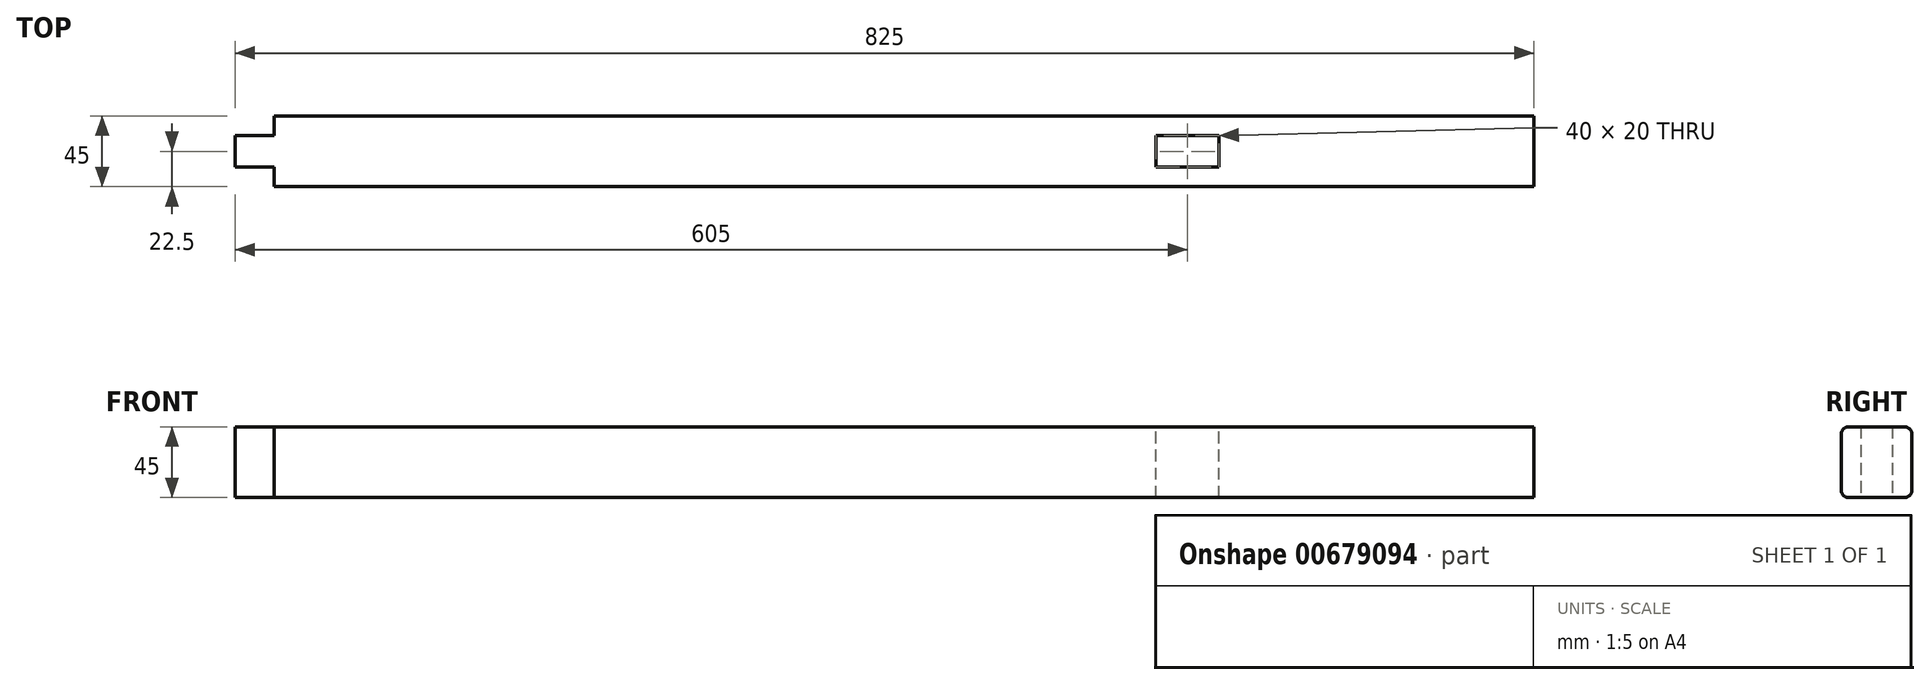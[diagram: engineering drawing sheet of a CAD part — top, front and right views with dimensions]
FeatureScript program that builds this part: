
annotation { "Feature Type Name" : "Feature", "Feature Type Description" : "" }
export const myFeature = defineFeature(function(context is Context, id is Id, definition is map)
    precondition{}
    {
        {
            var Q0;
            Q0=qCreatedBy(makeId("Right.planeOp"),FACE);
            var sketch = newSketch(context, id + "F0", { "sketchPlane" : qUnion([Q0])});
            skLineSegment(sketch, "E0.bottom", {"start": v(22.5, 22.5) * mm, "end": v(-22.5, 22.5) * mm});
            skLineSegment(sketch, "E0.top", {"start": v(22.5, -22.5) * mm, "end": v(-22.5, -22.5) * mm});
            skLineSegment(sketch, "E0.left", {"start": v(22.5, 22.5) * mm, "end": v(22.5, -22.5) * mm});
            skLineSegment(sketch, "E0.right", {"start": v(-22.5, 22.5) * mm, "end": v(-22.5, -22.5) * mm});
            skPoint(sketch, "E0.middle", {"position": v(0, 0) * mm});
            skSolve(sketch);
        }
        {
            var Q0;
            Q0 = qSketchRegion(id + "F0", true);
            extrude(context, id + "F1", {"entities" : qUnion([Q0]), "endBound" : BoundingType.SYMMETRIC, "depth" : 800 * mm, "offsetDistance" : 25 * mm});
        }
        {
            var Q0;
            Q0=makeQuery(id+"F1.opExtrude","CAP_FACE",FACE,{"disambiguationData":[OSD([sQuery(id+"F0.wireOp",EDGE,"E0.bottom"),sQuery(id+"F0.wireOp",EDGE,"E0.top"),sQuery(id+"F0.wireOp",EDGE,"E0.left"),sQuery(id+"F0.wireOp",EDGE,"E0.right")])],"isStart":true});
            var sketch = newSketch(context, id + "F2", { "sketchPlane" : qUnion([Q0])});
            skLineSegment(sketch, "E1.bottom", {"start": v(10, 22.5) * mm, "end": v(-10, 22.5) * mm});
            skLineSegment(sketch, "E1.top", {"start": v(10, -22.5) * mm, "end": v(-10, -22.5) * mm});
            skLineSegment(sketch, "E1.left", {"start": v(10, 22.5) * mm, "end": v(10, -22.5) * mm});
            skLineSegment(sketch, "E1.right", {"start": v(-10, 22.5) * mm, "end": v(-10, -22.5) * mm});
            skPoint(sketch, "E1.middle", {"position": v(0, 0) * mm});
            skSolve(sketch);
        }
        {
            var Q0;
            Q0 = qSketchRegion(id + "F2", true);
            extrude(context, id + "F3", {"entities" : qUnion([Q0]), "operationType" : NewBodyOperationType.ADD, "depth" : 25 * mm, "offsetDistance" : 25 * mm});
        }
        {
            var Q0;
            Q0=makeQuery(id+"F1.opExtrude","SWEPT_EDGE",EDGE,{"disambiguationData":[OSD([sQuery(id+"F0.wireOp",EDGE,"E0.top"),sQuery(id+"F0.wireOp",EDGE,"E0.right")])]});
            var Q1;
            Q1=makeQuery(id+"F1.opExtrude","SWEPT_EDGE",EDGE,{"disambiguationData":[OSD([sQuery(id+"F0.wireOp",EDGE,"E0.top"),sQuery(id+"F0.wireOp",EDGE,"E0.left")])]});
            var Q2;
            Q2=makeQuery(id+"F1.opExtrude","SWEPT_EDGE",EDGE,{"disambiguationData":[OSD([sQuery(id+"F0.wireOp",EDGE,"E0.bottom"),sQuery(id+"F0.wireOp",EDGE,"E0.right")])]});
            var Q3;
            Q3=makeQuery(id+"F1.opExtrude","SWEPT_EDGE",EDGE,{"disambiguationData":[OSD([sQuery(id+"F0.wireOp",EDGE,"E0.bottom"),sQuery(id+"F0.wireOp",EDGE,"E0.left")])]});
            fillet(context, id + "F4", {"entities" : qUnion([Q0, Q1, Q2, Q3]), "radius" : 5 * mm, "tangentPropagation" : true, "allowEdgeOverflow" : false});
        }
        {
            var Q0;
            Q0=makeQuery(id+"F3.boolean.opBoolean","MERGE",FACE,{"derivedFrom":[makeQuery(id+"F1.opExtrude","SWEPT_FACE",FACE,{"disambiguationData":[OSD([sQuery(id+"F0.wireOp",EDGE,"E0.bottom")])]}),makeQuery(id+"F3.opExtrude","SWEPT_FACE",FACE,{"disambiguationData":[OSD([sQuery(id+"F2.wireOp",EDGE,"E1.bottom")])]})]});
            var sketch = newSketch(context, id + "F5", { "sketchPlane" : qUnion([Q0])});
            skLineSegment(sketch, "E2.bottom", {"start": v(200, 10) * mm, "end": v(160, 10) * mm});
            skLineSegment(sketch, "E2.top", {"start": v(200, -10) * mm, "end": v(160, -10) * mm});
            skLineSegment(sketch, "E2.left", {"start": v(200, 10) * mm, "end": v(200, -10) * mm});
            skLineSegment(sketch, "E2.right", {"start": v(160, 10) * mm, "end": v(160, -10) * mm});
            skPoint(sketch, "E2.middle", {"position": v(180, 0) * mm});
            skSolve(sketch);
        }
        {
            var Q0;
            Q0 = qSketchRegion(id + "F5", true);
            extrude(context, id + "F6", {"entities" : qUnion([Q0]), "operationType" : NewBodyOperationType.REMOVE, "endBound" : BoundingType.THROUGH_ALL, "oppositeDirection" : true, "depth" : 25 * mm, "offsetDistance" : 25 * mm});
        }
    });
